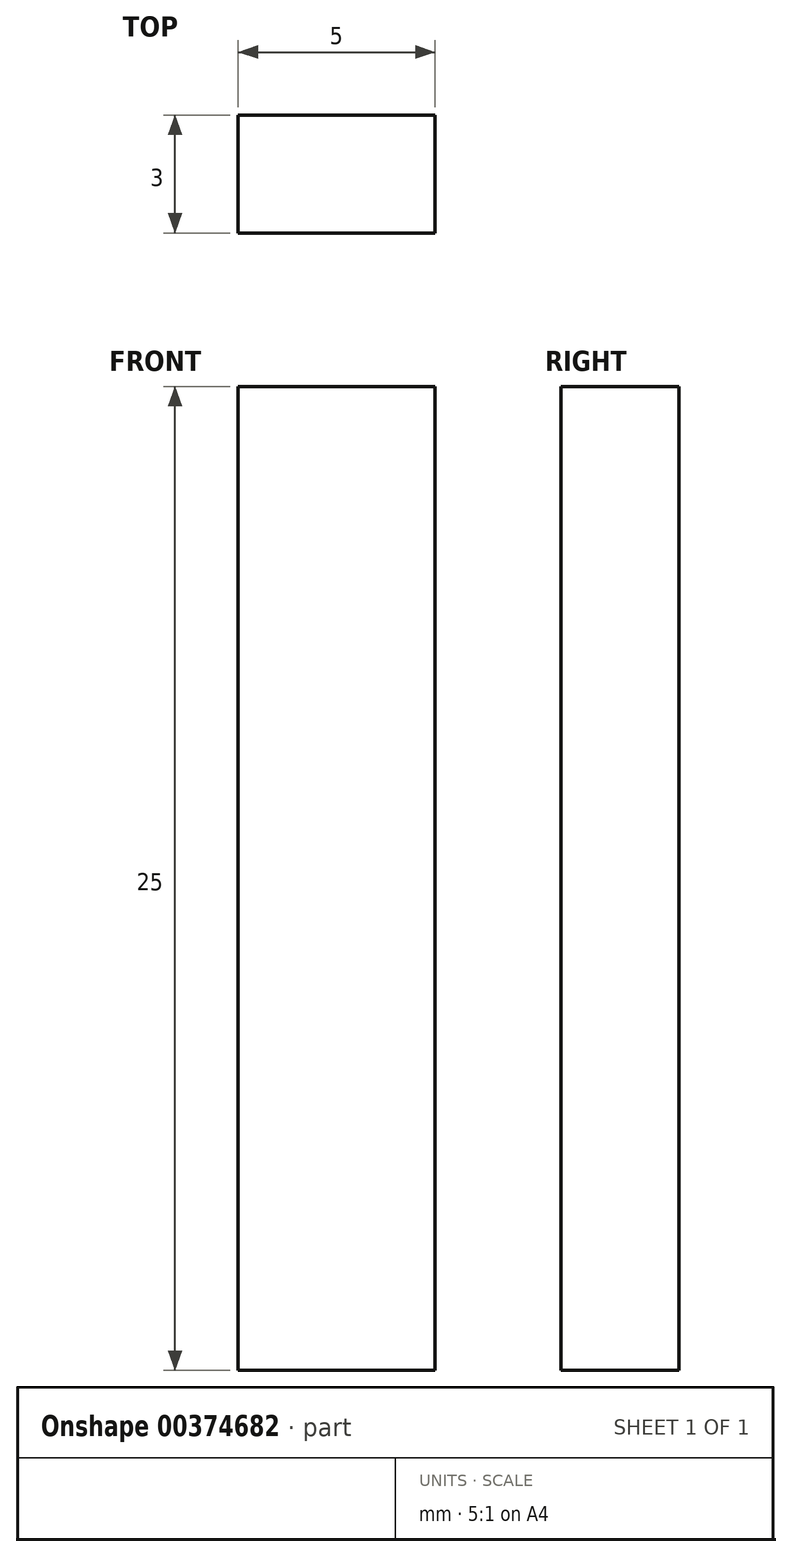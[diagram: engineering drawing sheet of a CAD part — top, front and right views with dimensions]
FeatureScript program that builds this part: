
annotation { "Feature Type Name" : "Feature", "Feature Type Description" : "" }
export const myFeature = defineFeature(function(context is Context, id is Id, definition is map)
    precondition{}
    {
        {
            var Q0;
            Q0=qCreatedBy(makeId("Top.planeOp"),FACE);
            var sketch = newSketch(context, id + "F0", { "sketchPlane" : qUnion([Q0])});
            skLineSegment(sketch, "E0.bottom", {"start": v(2.5, 1.5) * mm, "end": v(-2.5, 1.5) * mm});
            skLineSegment(sketch, "E0.top", {"start": v(2.5, -1.5) * mm, "end": v(-2.5, -1.5) * mm});
            skLineSegment(sketch, "E0.left", {"start": v(2.5, 1.5) * mm, "end": v(2.5, -1.5) * mm});
            skLineSegment(sketch, "E0.right", {"start": v(-2.5, 1.5) * mm, "end": v(-2.5, -1.5) * mm});
            skPoint(sketch, "E0.middle", {"position": v(0, 0) * mm});
            skSolve(sketch);
        }
        {
            var Q0;
            Q0=makeQuery(id+"F0.imprint","IMPRINT",FACE,{"disambiguationData":[TD([[makeQuery(id+"F0.imprint","IMPRINT",EDGE,{"derivedFrom":sQuery(id+"F0.wireOp",EDGE,"E0.bottom")}),1.0]])]});
            extrude(context, id + "F1", {"entities" : qUnion([Q0]), "depth" : 25 * mm});
        }
    });
